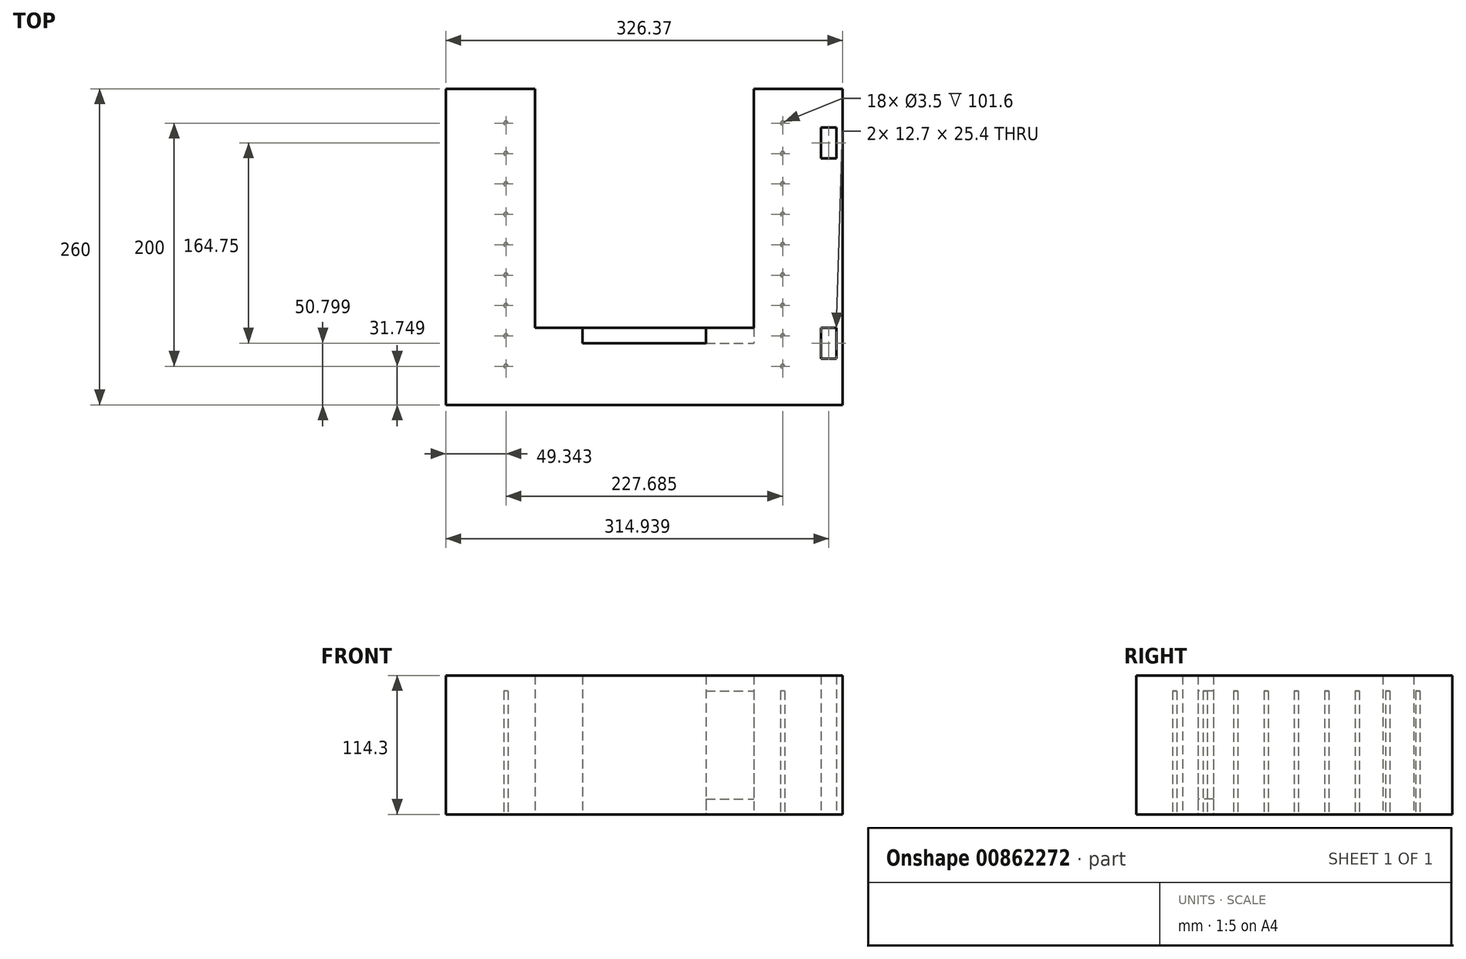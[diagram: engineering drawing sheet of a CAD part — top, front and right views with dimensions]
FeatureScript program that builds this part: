
annotation { "Feature Type Name" : "Feature", "Feature Type Description" : "" }
export const myFeature = defineFeature(function(context is Context, id is Id, definition is map)
    precondition{}
    {
        {
            assignVariable(context, id + "F0", {"name" : "thickness", "anyValue" : 12.7 * mm});
        }
        {
            var Q0;
            Q0=qCreatedBy(makeId("Top.planeOp"),FACE);
            var sketch = newSketch(context, id + "F1", { "sketchPlane" : qUnion([Q0])});
            skLineSegment(sketch, "E0.bottom", {"start": v(-201.4, 152.78) * mm, "end": v(124.96, 152.78) * mm});
            skLineSegment(sketch, "E0.top", {"start": v(-201.4, -107.22) * mm, "end": v(124.96, -107.22) * mm});
            skLineSegment(sketch, "E0.left", {"start": v(-201.4, 152.78) * mm, "end": v(-201.4, -107.22) * mm});
            skLineSegment(sketch, "E0.right", {"start": v(124.96, 152.78) * mm, "end": v(124.96, -107.22) * mm});
            skPoint(sketch, "E0.middle", {"position": v(-38.22, 22.78) * mm});
            skLineSegment(sketch, "E1.bottom", {"start": v(-128.22, 152.78) * mm, "end": v(51.78, 152.78) * mm});
            skLineSegment(sketch, "E1.top", {"start": v(-128.22, -43.72) * mm, "end": v(51.78, -43.72) * mm});
            skLineSegment(sketch, "E1.left", {"start": v(-128.22, 152.78) * mm, "end": v(-128.22, -43.72) * mm});
            skLineSegment(sketch, "E1.right", {"start": v(51.78, 152.78) * mm, "end": v(51.78, -43.72) * mm});
            skPoint(sketch, "E1.middle", {"position": v(-38.22, 54.53) * mm});
            skLineSegment(sketch, "E2", {"start": v(-38.22, 216.28) * mm, "end": v(-38.22, -107.22) * mm, "construction": true});
            skPoint(sketch, "E3", {"position": v(-152.07, -75.47) * mm});
            skCircle(sketch, "E4", {"center": v(-152.07, -75.47) * mm, "radius": 1.75 * mm});
            skPoint(sketch, "E5.0.1.0", {"position": v(-152.07, -50.47) * mm});
            skCircle(sketch, "E5.0.1.1", {"center": v(-152.07, -50.47) * mm, "radius": 1.75 * mm});
            skPoint(sketch, "E5.0.2.0", {"position": v(-152.07, -25.47) * mm});
            skCircle(sketch, "E5.0.2.1", {"center": v(-152.07, -25.47) * mm, "radius": 1.75 * mm});
            skPoint(sketch, "E5.0.3.0", {"position": v(-152.07, -0.47) * mm});
            skCircle(sketch, "E5.0.3.1", {"center": v(-152.07, -0.47) * mm, "radius": 1.75 * mm});
            skPoint(sketch, "E5.0.4.0", {"position": v(-152.07, 24.53) * mm});
            skCircle(sketch, "E5.0.4.1", {"center": v(-152.07, 24.53) * mm, "radius": 1.75 * mm});
            skPoint(sketch, "E5.0.5.0", {"position": v(-152.07, 49.53) * mm});
            skCircle(sketch, "E5.0.5.1", {"center": v(-152.07, 49.53) * mm, "radius": 1.75 * mm});
            skPoint(sketch, "E5.0.6.0", {"position": v(-152.07, 74.53) * mm});
            skCircle(sketch, "E5.0.6.1", {"center": v(-152.07, 74.53) * mm, "radius": 1.75 * mm});
            skPoint(sketch, "E5.0.7.0", {"position": v(-152.07, 99.53) * mm});
            skCircle(sketch, "E5.0.7.1", {"center": v(-152.07, 99.53) * mm, "radius": 1.75 * mm});
            skLineSegment(sketch, "E5.direction1", {"start": v(-152.07, -75.47) * mm, "end": v(-126.67, -75.47) * mm, "construction": true});
            skLineSegment(sketch, "E5.direction2", {"start": v(-152.07, -75.47) * mm, "end": v(-152.07, -50.47) * mm, "construction": true});
            skPoint(sketch, "E6.0.0.8", {"position": v(-152.07, 124.53) * mm});
            skCircle(sketch, "E6.1.0.8", {"center": v(-152.07, 124.53) * mm, "radius": 1.75 * mm});
            skCircle(sketch, "E7.MirrorC", {"center": v(75.62, -75.47) * mm, "radius": 1.75 * mm});
            skCircle(sketch, "E8.MirrorC", {"center": v(75.62, -25.47) * mm, "radius": 1.75 * mm});
            skCircle(sketch, "E9.MirrorC", {"center": v(75.62, 99.53) * mm, "radius": 1.75 * mm});
            skCircle(sketch, "E10.MirrorC", {"center": v(75.62, -0.47) * mm, "radius": 1.75 * mm});
            skCircle(sketch, "E11.MirrorC", {"center": v(75.62, 74.53) * mm, "radius": 1.75 * mm});
            skCircle(sketch, "E12.MirrorC", {"center": v(75.62, 49.53) * mm, "radius": 1.75 * mm});
            skCircle(sketch, "E13.MirrorC", {"center": v(75.62, 124.53) * mm, "radius": 1.75 * mm});
            skCircle(sketch, "E14.MirrorC", {"center": v(75.62, 24.53) * mm, "radius": 1.75 * mm});
            skCircle(sketch, "E15.MirrorC", {"center": v(75.62, -50.47) * mm, "radius": 1.75 * mm});
            skLineSegment(sketch, "E16", {"start": v(-201.4, 22.78) * mm, "end": v(124.96, 22.78) * mm, "construction": true});
            skLineSegment(sketch, "E17.bottom", {"start": v(-197.58, 121.03) * mm, "end": v(-184.88, 121.03) * mm});
            skLineSegment(sketch, "E17.top", {"start": v(-197.58, 95.63) * mm, "end": v(-184.88, 95.63) * mm});
            skLineSegment(sketch, "E17.left", {"start": v(-197.58, 121.03) * mm, "end": v(-197.58, 95.63) * mm});
            skLineSegment(sketch, "E17.right", {"start": v(-184.88, 121.03) * mm, "end": v(-184.88, 95.63) * mm});
            skPoint(sketch, "E17.middle", {"position": v(-191.23, 108.33) * mm});
            skLineSegment(sketch, "E18.bottom", {"start": v(119.88, 121.03) * mm, "end": v(107.18, 121.03) * mm});
            skLineSegment(sketch, "E18.top", {"start": v(119.88, 95.63) * mm, "end": v(107.18, 95.63) * mm});
            skLineSegment(sketch, "E18.left", {"start": v(119.88, 121.03) * mm, "end": v(119.88, 95.63) * mm});
            skLineSegment(sketch, "E18.right", {"start": v(107.18, 121.03) * mm, "end": v(107.18, 95.63) * mm});
            skPoint(sketch, "E18.middle", {"position": v(113.53, 108.33) * mm});
            skPoint(sketch, "E18.middle.positionSnap0", {"position": v(-184.88, 108.33) * mm});
            skPoint(sketch, "E18.centerSnap0", {"position": v(-184.88, 108.33) * mm});
            skLineSegment(sketch, "E19.bottom", {"start": v(119.88, -43.72) * mm, "end": v(107.18, -43.72) * mm});
            skLineSegment(sketch, "E19.top", {"start": v(119.88, -69.12) * mm, "end": v(107.18, -69.12) * mm});
            skLineSegment(sketch, "E19.left", {"start": v(119.88, -43.72) * mm, "end": v(119.88, -69.12) * mm});
            skLineSegment(sketch, "E19.right", {"start": v(107.18, -43.72) * mm, "end": v(107.18, -69.12) * mm});
            skPoint(sketch, "E19.middle", {"position": v(113.53, -56.42) * mm});
            skLineSegment(sketch, "E20.bottom", {"start": v(-197.58, -43.72) * mm, "end": v(-184.88, -43.72) * mm});
            skLineSegment(sketch, "E20.top", {"start": v(-197.58, -69.12) * mm, "end": v(-184.88, -69.12) * mm});
            skLineSegment(sketch, "E20.left", {"start": v(-197.58, -43.72) * mm, "end": v(-197.58, -69.12) * mm});
            skLineSegment(sketch, "E20.right", {"start": v(-184.88, -43.72) * mm, "end": v(-184.88, -69.12) * mm});
            skPoint(sketch, "E20.middle", {"position": v(-191.23, -56.42) * mm});
            skLineSegment(sketch, "E21.bottom", {"start": v(-89.02, -43.72) * mm, "end": v(12.58, -43.72) * mm});
            skLineSegment(sketch, "E21.top", {"start": v(-89.02, -56.42) * mm, "end": v(12.58, -56.42) * mm});
            skLineSegment(sketch, "E21.left", {"start": v(-89.02, -43.72) * mm, "end": v(-89.02, -56.42) * mm});
            skLineSegment(sketch, "E21.right", {"start": v(12.58, -43.72) * mm, "end": v(12.58, -56.42) * mm});
            skPoint(sketch, "E21.middle", {"position": v(-38.22, -50.07) * mm});
            skPoint(sketch, "E22", {"position": v(-38.22, -43.72) * mm});
            skSolve(sketch);
        }
        {
            var Q0;
            Q0=makeQuery(id+"F1.imprint","IMPRINT",FACE,{"disambiguationData":[TD([[makeQuery(id+"F1.imprint","IMPRINT",EDGE,{"derivedFrom":sQuery(id+"F1.wireOp",EDGE,"E0.top")}),1.0]])]});
            extrude(context, id + "F2", {"entities" : qUnion([Q0]), "depth" : getVariable(context, 'thickness'), "offsetDistance" : 25.4 * mm});
        }
        {
            var Q0;
            Q0=makeQuery(id+"F2.opExtrude","CAP_FACE",FACE,{"disambiguationData":[OSD([sQuery(id+"F1.wireOp",EDGE,"E0.bottom"),sQuery(id+"F1.wireOp",EDGE,"E0.top"),sQuery(id+"F1.wireOp",EDGE,"E0.left"),sQuery(id+"F1.wireOp",EDGE,"E0.right"),sQuery(id+"F1.wireOp",EDGE,"E1.top"),sQuery(id+"F1.wireOp",EDGE,"E1.left"),sQuery(id+"F1.wireOp",EDGE,"E1.right"),sQuery(id+"F1.wireOp",EDGE,"E4"),sQuery(id+"F1.wireOp",EDGE,"E5.0.1.1"),sQuery(id+"F1.wireOp",EDGE,"E5.0.2.1"),sQuery(id+"F1.wireOp",EDGE,"E5.0.3.1"),sQuery(id+"F1.wireOp",EDGE,"E5.0.4.1"),sQuery(id+"F1.wireOp",EDGE,"E5.0.5.1"),sQuery(id+"F1.wireOp",EDGE,"E5.0.6.1"),sQuery(id+"F1.wireOp",EDGE,"E5.0.7.1"),sQuery(id+"F1.wireOp",EDGE,"E6.1.0.8"),sQuery(id+"F1.wireOp",EDGE,"E7.MirrorC"),sQuery(id+"F1.wireOp",EDGE,"E8.MirrorC"),sQuery(id+"F1.wireOp",EDGE,"E9.MirrorC"),sQuery(id+"F1.wireOp",EDGE,"E10.MirrorC"),sQuery(id+"F1.wireOp",EDGE,"E11.MirrorC"),sQuery(id+"F1.wireOp",EDGE,"E12.MirrorC"),sQuery(id+"F1.wireOp",EDGE,"E13.MirrorC"),sQuery(id+"F1.wireOp",EDGE,"E14.MirrorC"),sQuery(id+"F1.wireOp",EDGE,"E15.MirrorC"),sQuery(id+"F1.wireOp",EDGE,"E17.bottom"),sQuery(id+"F1.wireOp",EDGE,"E17.top"),sQuery(id+"F1.wireOp",EDGE,"E17.left"),sQuery(id+"F1.wireOp",EDGE,"E17.right"),sQuery(id+"F1.wireOp",EDGE,"E18.bottom"),sQuery(id+"F1.wireOp",EDGE,"E18.top"),sQuery(id+"F1.wireOp",EDGE,"E18.left"),sQuery(id+"F1.wireOp",EDGE,"E18.right"),sQuery(id+"F1.wireOp",EDGE,"E19.bottom"),sQuery(id+"F1.wireOp",EDGE,"E19.top"),sQuery(id+"F1.wireOp",EDGE,"E19.left"),sQuery(id+"F1.wireOp",EDGE,"E19.right"),sQuery(id+"F1.wireOp",EDGE,"E20.bottom"),sQuery(id+"F1.wireOp",EDGE,"E20.top"),sQuery(id+"F1.wireOp",EDGE,"E20.left"),sQuery(id+"F1.wireOp",EDGE,"E20.right")])],"isStart":false});
            var sketch = newSketch(context, id + "F3", { "sketchPlane" : qUnion([Q0])});
            skLineSegment(sketch, "E23.0.0", {"start": v(-128.22, 152.78) * mm, "end": v(-201.4, 152.78) * mm, "construction": true});
            skLineSegment(sketch, "E23.0.1", {"start": v(-201.4, 152.78) * mm, "end": v(-201.4, -107.22) * mm, "construction": true});
            skLineSegment(sketch, "E23.0.2", {"start": v(-201.4, -107.22) * mm, "end": v(124.96, -107.22) * mm, "construction": true});
            skLineSegment(sketch, "E23.0.3", {"start": v(124.96, -107.22) * mm, "end": v(124.96, 152.78) * mm, "construction": true});
            skLineSegment(sketch, "E23.0.4", {"start": v(124.96, 152.78) * mm, "end": v(51.78, 152.78) * mm, "construction": true});
            skLineSegment(sketch, "E23.0.5", {"start": v(51.78, 152.78) * mm, "end": v(51.78, -43.72) * mm, "construction": true});
            skLineSegment(sketch, "E23.0.6", {"start": v(51.78, -43.72) * mm, "end": v(-128.22, -43.72) * mm, "construction": true});
            skLineSegment(sketch, "E23.0.7", {"start": v(-128.22, -43.72) * mm, "end": v(-128.22, 152.78) * mm, "construction": true});
            skLineSegment(sketch, "E24.0", {"start": v(-184.88, 121.03) * mm, "end": v(-184.88, 95.63) * mm, "construction": true});
            skLineSegment(sketch, "E24.1", {"start": v(-197.58, 121.03) * mm, "end": v(-197.58, 95.63) * mm, "construction": true});
            skLineSegment(sketch, "E25.0", {"start": v(-184.88, -43.72) * mm, "end": v(-184.88, -69.12) * mm, "construction": true});
            skLineSegment(sketch, "E25.1", {"start": v(-197.58, -43.72) * mm, "end": v(-197.58, -69.12) * mm, "construction": true});
            skPoint(sketch, "E26", {"position": v(-191.23, 108.33) * mm});
            skPoint(sketch, "E26.positionSnap0", {"position": v(-197.58, 108.33) * mm});
            skPoint(sketch, "E26.positionSnap1", {"position": v(-191.23, 121.03) * mm});
            skPoint(sketch, "E27.oppositeSnap0", {"position": v(-184.88, -56.42) * mm});
            skLineSegment(sketch, "E27.bottom", {"start": v(-197.58, 152.78) * mm, "end": v(-184.88, 152.78) * mm});
            skLineSegment(sketch, "E27.top", {"start": v(-197.58, -107.22) * mm, "end": v(-184.88, -107.22) * mm});
            skLineSegment(sketch, "E27.left", {"start": v(-197.58, 152.78) * mm, "end": v(-197.58, -107.22) * mm});
            skLineSegment(sketch, "E27.right", {"start": v(-184.88, 152.78) * mm, "end": v(-184.88, -107.22) * mm});
            skSolve(sketch);
        }
        {
            var Q0;
            {var subQ1=makeQuery(id+"F2.opExtrude","CAP_EDGE",EDGE,{"disambiguationData":[OSD([sQuery(id+"F1.wireOp",EDGE,"E17.top")])],"isStart":false});Q0=makeQuery(id+"F3.imprint","IMPRINT",FACE,{"disambiguationData":[TD([[makeQuery(id+"F3.imprint","IMPRINT",EDGE,{"derivedFrom":subQ1}),-1.0]])]});}
            var Q1;
            {var subQ0=sQuery(id+"F3.wireOp",EDGE,"E27.top");Q1=makeQuery(id+"F3.imprint","IMPRINT",FACE,{"disambiguationData":[TD([[makeQuery(id+"F3.imprint","IMPRINT",EDGE,{"derivedFrom":subQ0}),1.0]])]});}
            var Q2;
            {var subQ1=makeQuery(id+"F2.opExtrude","CAP_EDGE",EDGE,{"disambiguationData":[OSD([sQuery(id+"F1.wireOp",EDGE,"E17.bottom")])],"isStart":false});Q2=makeQuery(id+"F3.imprint","IMPRINT",FACE,{"disambiguationData":[TD([[makeQuery(id+"F3.imprint","IMPRINT",EDGE,{"derivedFrom":subQ1}),-1.0]])]});}
            var Q3;
            {var subQ0=sQuery(id+"F3.wireOp",EDGE,"E27.bottom");Q3=makeQuery(id+"F3.imprint","IMPRINT",FACE,{"disambiguationData":[TD([[makeQuery(id+"F3.imprint","IMPRINT",EDGE,{"derivedFrom":subQ0}),-1.0]])]});}
            var Q4;
            {var subQ1=makeQuery(id+"F2.opExtrude","CAP_EDGE",EDGE,{"disambiguationData":[OSD([sQuery(id+"F1.wireOp",EDGE,"E20.bottom")])],"isStart":false});Q4=makeQuery(id+"F3.imprint","IMPRINT",FACE,{"disambiguationData":[TD([[makeQuery(id+"F3.imprint","IMPRINT",EDGE,{"derivedFrom":subQ1}),-1.0]])]});}
            extrude(context, id + "F4", {"entities" : qUnion([Q0, Q1, Q2, Q3, Q4]), "depth" : 88.9 * mm, "offsetDistance" : 25.4 * mm});
        }
        {
            var Q0;
            {var subQ1=makeQuery(id+"F2.opExtrude","CAP_EDGE",EDGE,{"disambiguationData":[OSD([sQuery(id+"F1.wireOp",EDGE,"E20.bottom")])],"isStart":false});Q0=makeQuery(id+"F3.imprint","IMPRINT",FACE,{"disambiguationData":[TD([[makeQuery(id+"F3.imprint","IMPRINT",EDGE,{"derivedFrom":subQ1}),-1.0]])]});}
            var Q1;
            {var subQ1=makeQuery(id+"F2.opExtrude","CAP_EDGE",EDGE,{"disambiguationData":[OSD([sQuery(id+"F1.wireOp",EDGE,"E17.bottom")])],"isStart":false});Q1=makeQuery(id+"F3.imprint","IMPRINT",FACE,{"disambiguationData":[TD([[makeQuery(id+"F3.imprint","IMPRINT",EDGE,{"derivedFrom":subQ1}),-1.0]])]});}
            var Q2;
            Q2=makeQuery(id+"F2.opExtrude","CAP_FACE",FACE,{"disambiguationData":[OSD([sQuery(id+"F1.wireOp",EDGE,"E0.bottom"),sQuery(id+"F1.wireOp",EDGE,"E0.top"),sQuery(id+"F1.wireOp",EDGE,"E0.left"),sQuery(id+"F1.wireOp",EDGE,"E0.right"),sQuery(id+"F1.wireOp",EDGE,"E1.top"),sQuery(id+"F1.wireOp",EDGE,"E1.left"),sQuery(id+"F1.wireOp",EDGE,"E1.right"),sQuery(id+"F1.wireOp",EDGE,"E4"),sQuery(id+"F1.wireOp",EDGE,"E5.0.1.1"),sQuery(id+"F1.wireOp",EDGE,"E5.0.2.1"),sQuery(id+"F1.wireOp",EDGE,"E5.0.3.1"),sQuery(id+"F1.wireOp",EDGE,"E5.0.4.1"),sQuery(id+"F1.wireOp",EDGE,"E5.0.5.1"),sQuery(id+"F1.wireOp",EDGE,"E5.0.6.1"),sQuery(id+"F1.wireOp",EDGE,"E5.0.7.1"),sQuery(id+"F1.wireOp",EDGE,"E6.1.0.8"),sQuery(id+"F1.wireOp",EDGE,"E7.MirrorC"),sQuery(id+"F1.wireOp",EDGE,"E8.MirrorC"),sQuery(id+"F1.wireOp",EDGE,"E9.MirrorC"),sQuery(id+"F1.wireOp",EDGE,"E10.MirrorC"),sQuery(id+"F1.wireOp",EDGE,"E11.MirrorC"),sQuery(id+"F1.wireOp",EDGE,"E12.MirrorC"),sQuery(id+"F1.wireOp",EDGE,"E13.MirrorC"),sQuery(id+"F1.wireOp",EDGE,"E14.MirrorC"),sQuery(id+"F1.wireOp",EDGE,"E15.MirrorC"),sQuery(id+"F1.wireOp",EDGE,"E17.bottom"),sQuery(id+"F1.wireOp",EDGE,"E17.top"),sQuery(id+"F1.wireOp",EDGE,"E17.left"),sQuery(id+"F1.wireOp",EDGE,"E17.right"),sQuery(id+"F1.wireOp",EDGE,"E18.bottom"),sQuery(id+"F1.wireOp",EDGE,"E18.top"),sQuery(id+"F1.wireOp",EDGE,"E18.left"),sQuery(id+"F1.wireOp",EDGE,"E18.right"),sQuery(id+"F1.wireOp",EDGE,"E19.bottom"),sQuery(id+"F1.wireOp",EDGE,"E19.top"),sQuery(id+"F1.wireOp",EDGE,"E19.left"),sQuery(id+"F1.wireOp",EDGE,"E19.right"),sQuery(id+"F1.wireOp",EDGE,"E20.bottom"),sQuery(id+"F1.wireOp",EDGE,"E20.top"),sQuery(id+"F1.wireOp",EDGE,"E20.left"),sQuery(id+"F1.wireOp",EDGE,"E20.right")])],"isStart":true});
            extrude(context, id + "F5", {"entities" : qUnion([Q0, Q1]), "operationType" : NewBodyOperationType.ADD, "endBound" : BoundingType.UP_TO_SURFACE, "oppositeDirection" : true, "depth" : 25.4 * mm, "endBoundEntityFace" : qUnion([Q2]), "offsetDistance" : 25.4 * mm});
        }
        {
            var Q0;
            Q0=makeQuery(id+"F4.opExtrude","CAP_FACE",FACE,{"disambiguationData":[OSD([sQuery(id+"F3.wireOp",EDGE,"E27.bottom"),sQuery(id+"F3.wireOp",EDGE,"E27.top"),sQuery(id+"F3.wireOp",EDGE,"E27.left"),sQuery(id+"F3.wireOp",EDGE,"E27.right")])],"isStart":false});
            var sketch = newSketch(context, id + "F6", { "sketchPlane" : qUnion([Q0])});
            skLineSegment(sketch, "E28.0", {"start": v(-201.4, 152.78) * mm, "end": v(-201.4, -107.22) * mm});
            skLineSegment(sketch, "E29.0", {"start": v(124.96, -107.22) * mm, "end": v(124.96, 152.78) * mm});
            skLineSegment(sketch, "E30.0", {"start": v(-201.4, -107.22) * mm, "end": v(124.96, -107.22) * mm});
            skLineSegment(sketch, "E31.0", {"start": v(-128.22, -43.72) * mm, "end": v(-89.02, -43.72) * mm});
            skLineSegment(sketch, "E32.0", {"start": v(12.58, -43.72) * mm, "end": v(51.78, -43.72) * mm});
            skLineSegment(sketch, "E33.0", {"start": v(12.58, -43.72) * mm, "end": v(12.58, -56.42) * mm});
            skLineSegment(sketch, "E34.0", {"start": v(-89.02, -43.72) * mm, "end": v(-89.02, -56.42) * mm});
            skLineSegment(sketch, "E35.0", {"start": v(-89.02, -56.42) * mm, "end": v(12.58, -56.42) * mm});
            skLineSegment(sketch, "E36.0", {"start": v(-128.22, 152.78) * mm, "end": v(-128.22, -43.72) * mm});
            skLineSegment(sketch, "E37.0", {"start": v(51.78, 152.78) * mm, "end": v(51.78, -43.72) * mm});
            skLineSegment(sketch, "E38.0", {"start": v(-201.4, 152.78) * mm, "end": v(-128.22, 152.78) * mm});
            skLineSegment(sketch, "E39.0", {"start": v(51.78, 152.78) * mm, "end": v(124.96, 152.78) * mm});
            skLineSegment(sketch, "E40.0", {"start": v(-197.58, 95.63) * mm, "end": v(-197.58, 121.03) * mm});
            skLineSegment(sketch, "E41.0", {"start": v(-197.58, 121.03) * mm, "end": v(-184.88, 121.03) * mm});
            skLineSegment(sketch, "E42.0", {"start": v(-184.88, 121.03) * mm, "end": v(-184.88, 95.63) * mm});
            skLineSegment(sketch, "E43.0", {"start": v(-197.58, 95.63) * mm, "end": v(-184.88, 95.63) * mm});
            skLineSegment(sketch, "E44.0", {"start": v(-197.58, -43.72) * mm, "end": v(-184.88, -43.72) * mm});
            skLineSegment(sketch, "E45.0", {"start": v(-184.88, -43.72) * mm, "end": v(-184.88, -69.12) * mm});
            skLineSegment(sketch, "E46.0", {"start": v(-197.58, -69.12) * mm, "end": v(-184.88, -69.12) * mm});
            skLineSegment(sketch, "E47.0", {"start": v(-197.58, -43.72) * mm, "end": v(-197.58, -69.12) * mm});
            skLineSegment(sketch, "E48.0", {"start": v(107.18, -43.72) * mm, "end": v(107.18, -69.12) * mm});
            skLineSegment(sketch, "E49.0", {"start": v(119.88, -69.12) * mm, "end": v(107.18, -69.12) * mm});
            skLineSegment(sketch, "E50.0", {"start": v(119.88, -43.72) * mm, "end": v(119.88, -69.12) * mm});
            skLineSegment(sketch, "E51.0", {"start": v(119.88, -43.72) * mm, "end": v(107.18, -43.72) * mm});
            skLineSegment(sketch, "E52.0", {"start": v(119.88, 95.63) * mm, "end": v(107.18, 95.63) * mm});
            skLineSegment(sketch, "E53.0", {"start": v(119.88, 121.03) * mm, "end": v(119.88, 95.63) * mm});
            skLineSegment(sketch, "E54.0", {"start": v(107.18, 121.03) * mm, "end": v(107.18, 95.63) * mm});
            skLineSegment(sketch, "E55.0", {"start": v(119.88, 121.03) * mm, "end": v(107.18, 121.03) * mm});
            skSolve(sketch);
        }
        {
            var Q0;
            {var subQ7=sQuery(id+"F6.wireOp",EDGE,"E29.0");Q0=makeQuery(id+"F6.imprint","IMPRINT",FACE,{"disambiguationData":[TD([[makeQuery(id+"F6.imprint","IMPRINT",EDGE,{"derivedFrom":subQ7}),1.0]])]});}
            var Q1;
            {var subQ5=sQuery(id+"F6.wireOp",EDGE,"E41.0");Q1=makeQuery(id+"F6.imprint","IMPRINT",FACE,{"disambiguationData":[TD([[makeQuery(id+"F6.imprint","IMPRINT",EDGE,{"derivedFrom":subQ5}),1.0]])]});}
            var Q2;
            {var subQ0=sQuery(id+"F6.wireOp",EDGE,"E43.0");Q2=makeQuery(id+"F6.imprint","IMPRINT",FACE,{"disambiguationData":[TD([[makeQuery(id+"F6.imprint","IMPRINT",EDGE,{"derivedFrom":subQ0}),-1.0]])]});}
            var Q3;
            {var subQ5=sQuery(id+"F6.wireOp",EDGE,"E46.0");Q3=makeQuery(id+"F6.imprint","IMPRINT",FACE,{"disambiguationData":[TD([[makeQuery(id+"F6.imprint","IMPRINT",EDGE,{"derivedFrom":subQ5}),-1.0]])]});}
            var Q4;
            {var subQ4=sQuery(id+"F6.wireOp",EDGE,"E28.0");Q4=makeQuery(id+"F6.imprint","IMPRINT",FACE,{"disambiguationData":[TD([[makeQuery(id+"F6.imprint","IMPRINT",EDGE,{"derivedFrom":subQ4}),1.0]])]});}
            extrude(context, id + "F7", {"entities" : qUnion([Q0, Q1, Q2, Q3, Q4]), "depth" : getVariable(context, 'thickness'), "offsetDistance" : 25.4 * mm});
        }
        {
            var Q0;
            Q0=makeQuery(id+"F5.opExtrude","CAP_FACE",FACE,{"disambiguationData":[OSD([sQuery(id+"F1.wireOp",EDGE,"E0.bottom"),sQuery(id+"F1.wireOp",EDGE,"E0.top"),sQuery(id+"F1.wireOp",EDGE,"E0.left"),sQuery(id+"F1.wireOp",EDGE,"E0.right"),sQuery(id+"F1.wireOp",EDGE,"E1.top"),sQuery(id+"F1.wireOp",EDGE,"E1.left"),sQuery(id+"F1.wireOp",EDGE,"E1.right"),sQuery(id+"F1.wireOp",EDGE,"E4"),sQuery(id+"F1.wireOp",EDGE,"E5.0.1.1"),sQuery(id+"F1.wireOp",EDGE,"E5.0.2.1"),sQuery(id+"F1.wireOp",EDGE,"E5.0.3.1"),sQuery(id+"F1.wireOp",EDGE,"E5.0.4.1"),sQuery(id+"F1.wireOp",EDGE,"E5.0.5.1"),sQuery(id+"F1.wireOp",EDGE,"E5.0.6.1"),sQuery(id+"F1.wireOp",EDGE,"E5.0.7.1"),sQuery(id+"F1.wireOp",EDGE,"E6.1.0.8"),sQuery(id+"F1.wireOp",EDGE,"E7.MirrorC"),sQuery(id+"F1.wireOp",EDGE,"E8.MirrorC"),sQuery(id+"F1.wireOp",EDGE,"E9.MirrorC"),sQuery(id+"F1.wireOp",EDGE,"E10.MirrorC"),sQuery(id+"F1.wireOp",EDGE,"E11.MirrorC"),sQuery(id+"F1.wireOp",EDGE,"E12.MirrorC"),sQuery(id+"F1.wireOp",EDGE,"E13.MirrorC"),sQuery(id+"F1.wireOp",EDGE,"E14.MirrorC"),sQuery(id+"F1.wireOp",EDGE,"E15.MirrorC"),sQuery(id+"F1.wireOp",EDGE,"E17.bottom"),sQuery(id+"F1.wireOp",EDGE,"E17.top"),sQuery(id+"F1.wireOp",EDGE,"E17.left"),sQuery(id+"F1.wireOp",EDGE,"E17.right"),sQuery(id+"F1.wireOp",EDGE,"E18.bottom"),sQuery(id+"F1.wireOp",EDGE,"E18.top"),sQuery(id+"F1.wireOp",EDGE,"E18.left"),sQuery(id+"F1.wireOp",EDGE,"E18.right"),sQuery(id+"F1.wireOp",EDGE,"E19.bottom"),sQuery(id+"F1.wireOp",EDGE,"E19.top"),sQuery(id+"F1.wireOp",EDGE,"E19.left"),sQuery(id+"F1.wireOp",EDGE,"E19.right"),sQuery(id+"F1.wireOp",EDGE,"E20.bottom"),sQuery(id+"F1.wireOp",EDGE,"E20.top"),sQuery(id+"F1.wireOp",EDGE,"E20.left"),sQuery(id+"F1.wireOp",EDGE,"E20.right"),sQuery(id+"F1.wireOp",EDGE,"E21.top"),sQuery(id+"F1.wireOp",EDGE,"E21.left"),sQuery(id+"F1.wireOp",EDGE,"E21.right")]),OD(0.0)],"isStart":false});
            var Q1;
            Q1=makeQuery(id+"F5.opExtrude","CAP_FACE",FACE,{"disambiguationData":[OSD([sQuery(id+"F1.wireOp",EDGE,"E0.bottom"),sQuery(id+"F1.wireOp",EDGE,"E0.top"),sQuery(id+"F1.wireOp",EDGE,"E0.left"),sQuery(id+"F1.wireOp",EDGE,"E0.right"),sQuery(id+"F1.wireOp",EDGE,"E1.top"),sQuery(id+"F1.wireOp",EDGE,"E1.left"),sQuery(id+"F1.wireOp",EDGE,"E1.right"),sQuery(id+"F1.wireOp",EDGE,"E4"),sQuery(id+"F1.wireOp",EDGE,"E5.0.1.1"),sQuery(id+"F1.wireOp",EDGE,"E5.0.2.1"),sQuery(id+"F1.wireOp",EDGE,"E5.0.3.1"),sQuery(id+"F1.wireOp",EDGE,"E5.0.4.1"),sQuery(id+"F1.wireOp",EDGE,"E5.0.5.1"),sQuery(id+"F1.wireOp",EDGE,"E5.0.6.1"),sQuery(id+"F1.wireOp",EDGE,"E5.0.7.1"),sQuery(id+"F1.wireOp",EDGE,"E6.1.0.8"),sQuery(id+"F1.wireOp",EDGE,"E7.MirrorC"),sQuery(id+"F1.wireOp",EDGE,"E8.MirrorC"),sQuery(id+"F1.wireOp",EDGE,"E9.MirrorC"),sQuery(id+"F1.wireOp",EDGE,"E10.MirrorC"),sQuery(id+"F1.wireOp",EDGE,"E11.MirrorC"),sQuery(id+"F1.wireOp",EDGE,"E12.MirrorC"),sQuery(id+"F1.wireOp",EDGE,"E13.MirrorC"),sQuery(id+"F1.wireOp",EDGE,"E14.MirrorC"),sQuery(id+"F1.wireOp",EDGE,"E15.MirrorC"),sQuery(id+"F1.wireOp",EDGE,"E17.bottom"),sQuery(id+"F1.wireOp",EDGE,"E17.top"),sQuery(id+"F1.wireOp",EDGE,"E17.left"),sQuery(id+"F1.wireOp",EDGE,"E17.right"),sQuery(id+"F1.wireOp",EDGE,"E18.bottom"),sQuery(id+"F1.wireOp",EDGE,"E18.top"),sQuery(id+"F1.wireOp",EDGE,"E18.left"),sQuery(id+"F1.wireOp",EDGE,"E18.right"),sQuery(id+"F1.wireOp",EDGE,"E19.bottom"),sQuery(id+"F1.wireOp",EDGE,"E19.top"),sQuery(id+"F1.wireOp",EDGE,"E19.left"),sQuery(id+"F1.wireOp",EDGE,"E19.right"),sQuery(id+"F1.wireOp",EDGE,"E20.bottom"),sQuery(id+"F1.wireOp",EDGE,"E20.top"),sQuery(id+"F1.wireOp",EDGE,"E20.left"),sQuery(id+"F1.wireOp",EDGE,"E20.right"),sQuery(id+"F1.wireOp",EDGE,"E21.top"),sQuery(id+"F1.wireOp",EDGE,"E21.left"),sQuery(id+"F1.wireOp",EDGE,"E21.right")]),OD(1.0)],"isStart":false});
            var Q2;
            Q2=makeQuery(id+"F7.opExtrude","CAP_FACE",FACE,{"disambiguationData":[OSD([sQuery(id+"F6.wireOp",EDGE,"E28.0"),sQuery(id+"F6.wireOp",EDGE,"E29.0"),sQuery(id+"F6.wireOp",EDGE,"E30.0"),sQuery(id+"F6.wireOp",EDGE,"E31.0"),sQuery(id+"F6.wireOp",EDGE,"E32.0"),sQuery(id+"F6.wireOp",EDGE,"E33.0"),sQuery(id+"F6.wireOp",EDGE,"E34.0"),sQuery(id+"F6.wireOp",EDGE,"E35.0"),sQuery(id+"F6.wireOp",EDGE,"E36.0"),sQuery(id+"F6.wireOp",EDGE,"E37.0"),sQuery(id+"F6.wireOp",EDGE,"E38.0"),sQuery(id+"F6.wireOp",EDGE,"E39.0"),sQuery(id+"F6.wireOp",EDGE,"E40.0"),sQuery(id+"F6.wireOp",EDGE,"E41.0"),sQuery(id+"F6.wireOp",EDGE,"E42.0"),sQuery(id+"F6.wireOp",EDGE,"E43.0"),sQuery(id+"F6.wireOp",EDGE,"E44.0"),sQuery(id+"F6.wireOp",EDGE,"E45.0"),sQuery(id+"F6.wireOp",EDGE,"E46.0"),sQuery(id+"F6.wireOp",EDGE,"E47.0"),sQuery(id+"F6.wireOp",EDGE,"E48.0"),sQuery(id+"F6.wireOp",EDGE,"E49.0"),sQuery(id+"F6.wireOp",EDGE,"E50.0"),sQuery(id+"F6.wireOp",EDGE,"E51.0"),sQuery(id+"F6.wireOp",EDGE,"E52.0"),sQuery(id+"F6.wireOp",EDGE,"E53.0"),sQuery(id+"F6.wireOp",EDGE,"E54.0"),sQuery(id+"F6.wireOp",EDGE,"E55.0")])],"isStart":false});
            extrude(context, id + "F8", {"entities" : qUnion([Q0, Q1]), "operationType" : NewBodyOperationType.ADD, "endBound" : BoundingType.UP_TO_SURFACE, "oppositeDirection" : true, "depth" : 25.4 * mm, "endBoundEntityFace" : qUnion([Q2]), "offsetDistance" : 25.4 * mm});
        }
        {
            var Q0;
            Q0=makeQuery(id+"F7.opExtrude","SWEPT_FACE",FACE,{"disambiguationData":[OSD([sQuery(id+"F6.wireOp",EDGE,"E35.0")])]});
            var sketch = newSketch(context, id + "F9", { "sketchPlane" : qUnion([Q0])});
            skLineSegment(sketch, "E56.0", {"start": v(-12.58, 101.6) * mm, "end": v(-51.78, 101.6) * mm});
            skPoint(sketch, "E57.0", {"position": v(-12.58, 107.95) * mm});
            skLineSegment(sketch, "E58.0", {"start": v(89.02, 114.3) * mm, "end": v(-12.58, 114.3) * mm});
            skLineSegment(sketch, "E59.0", {"start": v(89.02, 114.3) * mm, "end": v(89.02, 101.6) * mm});
            skLineSegment(sketch, "E60.0", {"start": v(128.22, 101.6) * mm, "end": v(89.02, 101.6) * mm});
            skLineSegment(sketch, "E61.0", {"start": v(128.22, 12.7) * mm, "end": v(89.02, 12.7) * mm});
            skLineSegment(sketch, "E62.0", {"start": v(89.02, 12.7) * mm, "end": v(89.02, 0) * mm});
            skLineSegment(sketch, "E63.0", {"start": v(89.02, 0) * mm, "end": v(-12.58, 0) * mm});
            skLineSegment(sketch, "E64.0", {"start": v(-12.58, 12.7) * mm, "end": v(-12.58, 0) * mm});
            skLineSegment(sketch, "E65.0", {"start": v(-12.58, 12.7) * mm, "end": v(-51.78, 12.7) * mm});
            skLineSegment(sketch, "E66", {"start": v(-51.78, 101.6) * mm, "end": v(-51.78, 12.7) * mm});
            skLineSegment(sketch, "E67", {"start": v(128.22, 101.6) * mm, "end": v(128.22, 12.7) * mm});
            skSolve(sketch);
        }
        {
            var Q0;
            Q0=makeQuery(id+"F9.imprint","IMPRINT",FACE,{"disambiguationData":[TD([[makeQuery(id+"F9.imprint","IMPRINT",EDGE,{"derivedFrom":sQuery(id+"F9.wireOp",EDGE,"E56.0")}),1.0]])]});
            var Q1;
            Q1=makeQuery(id+"F9.imprint","IMPRINT",FACE,{"disambiguationData":[TD([[makeQuery(id+"F9.imprint","IMPRINT",EDGE,{"derivedFrom":sQuery(id+"F9.wireOp",EDGE,"E58.0")}),1.0]])]});
            var Q2;
            {var subQ0=sQuery(id+"F1.wireOp",EDGE,"E1.top");Q2=makeQuery(id+"F2.opExtrude","SWEPT_FACE",FACE,{"disambiguationData":[OSD([subQ0]),TDD([makeQuery(id+"F1.imprint","IMPRINT",EDGE,{"disambiguationData":[TD([[makeQuery(id+"F1.imprint","INTERSECT",VERTEX,{"derivedFrom":[subQ0,sQuery(id+"F1.wireOp",EDGE,"E1.right")]}),1.0]])],"derivedFrom":subQ0})])]});}
            extrude(context, id + "F10", {"entities" : qUnion([Q0, Q1]), "endBound" : BoundingType.UP_TO_SURFACE, "depth" : 25.4 * mm, "endBoundEntityFace" : qUnion([Q2]), "offsetDistance" : 25.4 * mm});
        }
    });
